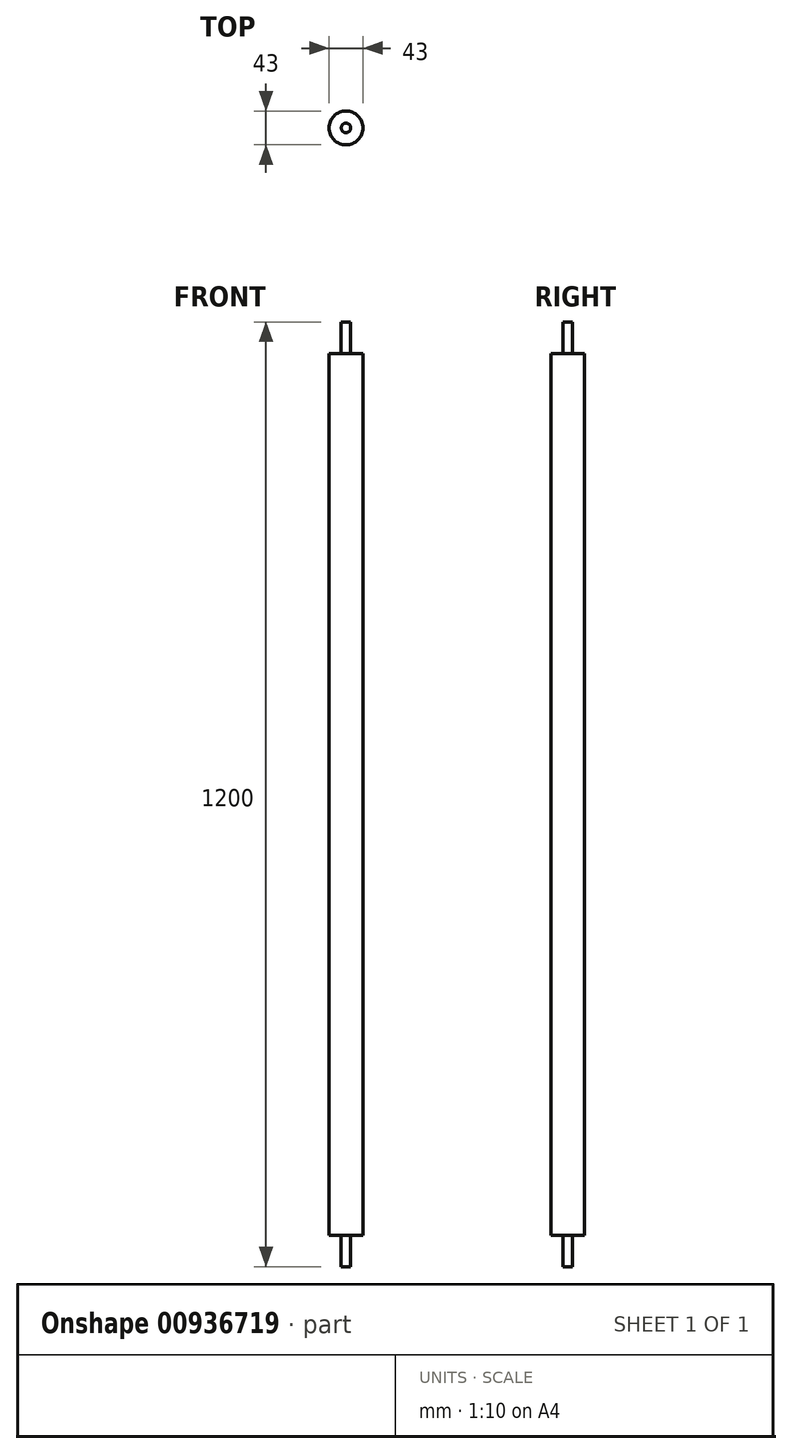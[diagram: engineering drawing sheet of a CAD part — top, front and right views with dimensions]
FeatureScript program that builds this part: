
annotation { "Feature Type Name" : "Feature", "Feature Type Description" : "" }
export const myFeature = defineFeature(function(context is Context, id is Id, definition is map)
    precondition{}
    {
        {
            var Q0;
            Q0=qCreatedBy(makeId("Top.planeOp"),FACE);
            var sketch = newSketch(context, id + "F0", { "sketchPlane" : qUnion([Q0])});
            skCircle(sketch, "E0", {"center": v(0, 0) * mm, "radius": 21.5 * mm});
            skSolve(sketch);
        }
        {
            var Q0;
            Q0 = qSketchRegion(id + "F0", true);
            extrude(context, id + "F1", {"entities" : qUnion([Q0]), "depth" : 1120 * mm, "offsetDistance" : 25 * mm});
        }
        {
            var Q0;
            Q0=makeQuery(id+"F1.opExtrude","CAP_FACE",FACE,{"disambiguationData":[OSD([sQuery(id+"F0.wireOp",EDGE,"E0")])],"isStart":true});
            var sketch = newSketch(context, id + "F2", { "sketchPlane" : qUnion([Q0])});
            skCircle(sketch, "E1", {"center": v(0, 0) * mm, "radius": 6 * mm});
            skSolve(sketch);
        }
        {
            var Q0;
            Q0 = qSketchRegion(id + "F2", true);
            extrude(context, id + "F3", {"entities" : qUnion([Q0]), "operationType" : NewBodyOperationType.ADD, "depth" : 40 * mm, "offsetDistance" : 25 * mm});
        }
        {
            var Q0;
            Q0=makeQuery(id+"F1.opExtrude","CAP_FACE",FACE,{"disambiguationData":[OSD([sQuery(id+"F0.wireOp",EDGE,"E0")])],"isStart":false});
            var sketch = newSketch(context, id + "F4", { "sketchPlane" : qUnion([Q0])});
            skCircle(sketch, "E2", {"center": v(0, 0) * mm, "radius": 6 * mm});
            skSolve(sketch);
        }
        {
            var Q0;
            Q0=makeQuery(id+"F4.imprint","IMPRINT",FACE,{"disambiguationData":[TD([[makeQuery(id+"F4.imprint","IMPRINT",EDGE,{"derivedFrom":sQuery(id+"F4.wireOp",EDGE,"E2")}),1.0]])]});
            extrude(context, id + "F5", {"entities" : qUnion([Q0]), "operationType" : NewBodyOperationType.ADD, "depth" : 40 * mm, "offsetDistance" : 25 * mm});
        }
    });
